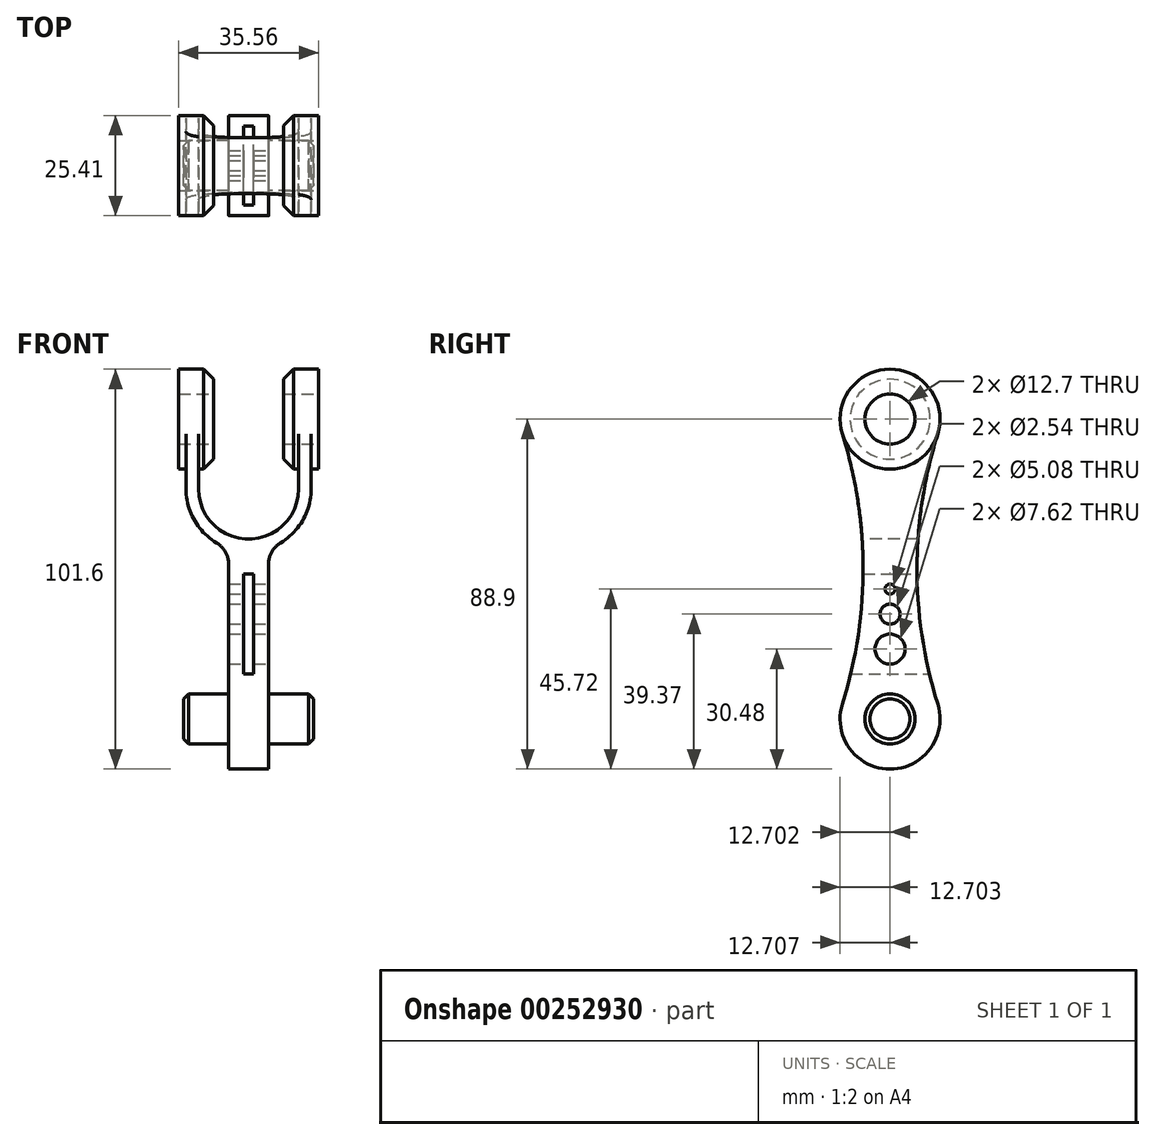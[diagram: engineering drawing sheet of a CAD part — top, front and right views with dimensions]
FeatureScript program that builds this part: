
annotation { "Feature Type Name" : "Feature", "Feature Type Description" : "" }
export const myFeature = defineFeature(function(context is Context, id is Id, definition is map)
    precondition{}
    {
        {
            var Q0;
            Q0=qCreatedBy(makeId("Front.planeOp"),FACE);
            var sketch = newSketch(context, id + "F0", { "sketchPlane" : qUnion([Q0])});
            skPoint(sketch, "E0.middle", {"position": v(0, 0) * mm});
            skArc(sketch, "E1", {"start": v(-8.17, -19.4) * mm, "mid": v(-13.82, -25.2) * mm, "end": v(-15.88, -33.02) * mm});
            skLineSegment(sketch, "E2.bottom", {"start": v(-5.08, 2.35) * mm, "end": v(5.08, 2.35) * mm});
            skLineSegment(sketch, "E2.left", {"start": v(-5.08, 2.35) * mm, "end": v(-5.08, -13.95) * mm});
            skLineSegment(sketch, "E2.right", {"start": v(5.08, 2.35) * mm, "end": v(5.08, -13.95) * mm});
            skArc(sketch, "E3", {"start": v(12.7, -33.02) * mm, "mid": v(0, -20.32) * mm, "end": v(-12.7, -33.02) * mm});
            skLineSegment(sketch, "E4.top", {"start": v(14.22, -50.8) * mm, "end": v(14.36, -50.8) * mm});
            skLineSegment(sketch, "E4.left", {"start": v(12.7, -33.02) * mm, "end": v(12.7, -49.28) * mm});
            skLineSegment(sketch, "E4.right", {"start": v(15.88, -33.02) * mm, "end": v(15.88, -49.28) * mm});
            skLineSegment(sketch, "E5.top", {"start": v(-14.36, -50.8) * mm, "end": v(-14.22, -50.8) * mm});
            skLineSegment(sketch, "E5.left", {"start": v(-15.88, -33.02) * mm, "end": v(-15.88, -49.28) * mm});
            skLineSegment(sketch, "E5.right", {"start": v(-12.7, -33.02) * mm, "end": v(-12.7, -49.28) * mm});
            skArc(sketch, "E6.trimOffspring", {"start": v(15.88, -33.02) * mm, "mid": v(13.82, -25.2) * mm, "end": v(8.17, -19.4) * mm});
            skPoint(sketch, "E7.visualSharp", {"position": v(-5.08, -17.97) * mm});
            skArc(sketch, "E7.filletArc", {"start": v(-8.17, -19.4) * mm, "mid": v(-5.9, -17.08) * mm, "end": v(-5.08, -13.95) * mm});
            skPoint(sketch, "E8.visualSharp", {"position": v(5.08, -17.97) * mm});
            skArc(sketch, "E8.filletArc", {"start": v(5.08, -13.95) * mm, "mid": v(5.9, -17.08) * mm, "end": v(8.17, -19.4) * mm});
            skArc(sketch, "E9.filletArc", {"start": v(12.7, -49.28) * mm, "mid": v(13.15, -50.35) * mm, "end": v(14.22, -50.8) * mm});
            skArc(sketch, "E10.filletArc", {"start": v(14.36, -50.8) * mm, "mid": v(15.44, -50.35) * mm, "end": v(15.88, -49.28) * mm});
            skArc(sketch, "E11.filletArc", {"start": v(-15.88, -49.28) * mm, "mid": v(-15.44, -50.35) * mm, "end": v(-14.36, -50.8) * mm});
            skArc(sketch, "E12.filletArc", {"start": v(-14.22, -50.8) * mm, "mid": v(-13.15, -50.35) * mm, "end": v(-12.7, -49.28) * mm});
            skSolve(sketch);
        }
        {
            var Q0;
            Q0=qSketchRegion(id+"F0",true);
            extrude(context, id + "F1", {"entities" : qUnion([Q0]), "endBound" : BoundingType.SYMMETRIC, "depth" : 38.1 * mm});
        }
        {
            var Q0;
            Q0=qCreatedBy(makeId("Right.planeOp"),FACE);
            var sketch = newSketch(context, id + "F2", { "sketchPlane" : qUnion([Q0])});
            skCircle(sketch, "E13", {"center": v(0, -50.8) * mm, "radius": 6.35 * mm});
            skSolve(sketch);
        }
        {
            var Q0;
            Q0=qCreatedBy(makeId("Right.planeOp"),FACE);
            var sketch = newSketch(context, id + "F3", { "sketchPlane" : qUnion([Q0])});
            skCircle(sketch, "E14", {"center": v(0, -50.8) * mm, "radius": 12.7 * mm});
            skSolve(sketch);
        }
        {
            var Q0;
            Q0 = qSketchRegion(id + "F3", true);
            extrude(context, id + "F4", {"entities" : qUnion([Q0]), "operationType" : NewBodyOperationType.ADD, "endBound" : BoundingType.SYMMETRIC, "depth" : 35.56 * mm});
        }
        {
            var Q0;
            Q0=qCreatedBy(makeId("Front.planeOp"),FACE);
            var sketch = newSketch(context, id + "F5", { "sketchPlane" : qUnion([Q0])});
            skLineSegment(sketch, "E15.bottom", {"start": v(8.9, -69.85) * mm, "end": v(-8.89, -69.85) * mm});
            skLineSegment(sketch, "E15.top", {"start": v(8.9, -31.75) * mm, "end": v(-8.89, -31.75) * mm});
            skLineSegment(sketch, "E15.left", {"start": v(8.9, -69.85) * mm, "end": v(8.9, -31.75) * mm});
            skLineSegment(sketch, "E15.right", {"start": v(-8.89, -69.85) * mm, "end": v(-8.89, -31.75) * mm});
            skPoint(sketch, "E15.middle", {"position": v(0, -50.8) * mm});
            skSolve(sketch);
        }
        {
            var Q0;
            Q0=qSketchRegion(id+"F2",true);
            extrude(context, id + "F6", {"entities" : qUnion([Q0]), "operationType" : NewBodyOperationType.REMOVE, "endBound" : BoundingType.SYMMETRIC, "oppositeDirection" : true, "depth" : 76.2 * mm});
        }
        {
            var Q0;
            Q0=qSketchRegion(id+"F5",true);
            extrude(context, id + "F7", {"entities" : qUnion([Q0]), "operationType" : NewBodyOperationType.REMOVE, "endBound" : BoundingType.SYMMETRIC, "oppositeDirection" : true, "depth" : 38.1 * mm});
        }
        {
            var Q0;
            Q0=makeQuery(id+"F7.boolean.opBoolean","INTERSECT",EDGE,{"derivedFrom":[makeQuery(id+"F4.opExtrude","SWEPT_FACE",FACE,{"disambiguationData":[OSD([sQuery(id+"F3.wireOp",EDGE,"E14")])]}),makeQuery(id+"F7.opExtrude","SWEPT_FACE",FACE,{"disambiguationData":[OSD([sQuery(id+"F5.wireOp",EDGE,"E15.right")])]})]});
            var Q1;
            Q1=makeQuery(id+"F7.boolean.opBoolean","INTERSECT",EDGE,{"derivedFrom":[makeQuery(id+"F4.opExtrude","SWEPT_FACE",FACE,{"disambiguationData":[OSD([sQuery(id+"F3.wireOp",EDGE,"E14")])]}),makeQuery(id+"F7.opExtrude","SWEPT_FACE",FACE,{"disambiguationData":[OSD([sQuery(id+"F5.wireOp",EDGE,"E15.left")])]})]});
            chamfer(context, id + "F8", {"entities" : qUnion([Q0, Q1]), "width" : 2.54 * mm, "tangentPropagation" : true});
        }
        {
            var Q0;
            Q0=qCreatedBy(makeId("Right.planeOp"),FACE);
            var sketch = newSketch(context, id + "F9", { "sketchPlane" : qUnion([Q0])});
            skArc(sketch, "E16", {"start": v(19.05, 25.39) * mm, "mid": v(0, 44.45) * mm, "end": v(-19.05, 25.39) * mm});
            skLineSegment(sketch, "E17.top", {"start": v(-19.05, -0.01) * mm, "end": v(19.05, -0.01) * mm});
            skLineSegment(sketch, "E17.left", {"start": v(-19.05, 25.39) * mm, "end": v(-19.05, -0.01) * mm});
            skLineSegment(sketch, "E17.right", {"start": v(19.05, 25.39) * mm, "end": v(19.05, -0.01) * mm});
            skSolve(sketch);
        }
        {
            var Q0;
            Q0=qSketchRegion(id+"F9",true);
            extrude(context, id + "F10", {"entities" : qUnion([Q0]), "operationType" : NewBodyOperationType.ADD, "endBound" : BoundingType.SYMMETRIC, "depth" : 10.16 * mm});
        }
        {
            var Q0;
            Q0=qCreatedBy(makeId("Right.planeOp"),FACE);
            var sketch = newSketch(context, id + "F11", { "sketchPlane" : qUnion([Q0])});
            skCircle(sketch, "E18", {"center": v(0, 25.4) * mm, "radius": 6.35 * mm});
            skSolve(sketch);
        }
        {
            var Q0;
            Q0=qSketchRegion(id+"F11",true);
            extrude(context, id + "F12", {"entities" : qUnion([Q0]), "operationType" : NewBodyOperationType.ADD, "endBound" : BoundingType.SYMMETRIC, "depth" : 33.02 * mm});
        }
        {
            var Q0;
            Q0=makeQuery(id+"F12.opExtrude","CAP_EDGE",EDGE,{"disambiguationData":[OSD([sQuery(id+"F11.wireOp",EDGE,"E18")])],"isStart":true});
            var Q1;
            Q1=makeQuery(id+"F12.opExtrude","CAP_EDGE",EDGE,{"disambiguationData":[OSD([sQuery(id+"F11.wireOp",EDGE,"E18")])],"isStart":false});
            chamfer(context, id + "F13", {"entities" : qUnion([Q0, Q1]), "width" : 1.27 * mm, "tangentPropagation" : true});
        }
        {
            var Q0;
            Q0=qCreatedBy(makeId("Right.planeOp"),FACE);
            var sketch = newSketch(context, id + "F14", { "sketchPlane" : qUnion([Q0])});
            skArc(sketch, "E19", {"start": v(12.12, 21.6) * mm, "mid": v(0, 38.1) * mm, "end": v(-12.12, 21.6) * mm});
            skArc(sketch, "E20", {"start": v(-12.12, -47) * mm, "mid": v(0, -63.5) * mm, "end": v(12.12, -47) * mm});
            skArc(sketch, "E21", {"start": v(12.12, 21.6) * mm, "mid": v(6.85, -12.7) * mm, "end": v(12.12, -47) * mm});
            skPoint(sketch, "E22.center.orphan", {"position": v(45.72, -6.35) * mm});
            skPoint(sketch, "E23.center.orphan", {"position": v(-45.72, -6.35) * mm});
            skArc(sketch, "E24", {"start": v(-12.12, -47) * mm, "mid": v(-6.85, -12.7) * mm, "end": v(-12.12, 21.6) * mm});
            skSolve(sketch);
        }
        {
            var Q0;
            Q0 = qSketchRegion(id + "F14", true);
            extrude(context, id + "F15", {"entities" : qUnion([Q0]), "operationType" : NewBodyOperationType.INTERSECT, "endBound" : BoundingType.SYMMETRIC, "depth" : 76.2 * mm});
        }
        {
            var Q0;
            Q0=qCreatedBy(makeId("Front.planeOp"),FACE);
            var sketch = newSketch(context, id + "F16", { "sketchPlane" : qUnion([Q0])});
            skLineSegment(sketch, "E25.bottom", {"start": v(-1.27, -11.4) * mm, "end": v(1.27, -11.4) * mm});
            skLineSegment(sketch, "E25.top", {"start": v(-1.27, 14) * mm, "end": v(1.27, 14) * mm});
            skLineSegment(sketch, "E25.left", {"start": v(-1.27, -11.4) * mm, "end": v(-1.27, 14) * mm});
            skLineSegment(sketch, "E25.right", {"start": v(1.27, -11.4) * mm, "end": v(1.27, 14) * mm});
            skSolve(sketch);
        }
        {
            var Q0;
            Q0=qSketchRegion(id+"F16",true);
            extrude(context, id + "F17", {"entities" : qUnion([Q0]), "operationType" : NewBodyOperationType.REMOVE, "endBound" : BoundingType.SYMMETRIC, "oppositeDirection" : true, "depth" : 50.8 * mm});
        }
        {
            var Q0;
            Q0=qCreatedBy(makeId("Right.planeOp"),FACE);
            var sketch = newSketch(context, id + "F18", { "sketchPlane" : qUnion([Q0])});
            skCircle(sketch, "E26", {"center": v(0, 7.62) * mm, "radius": 3.81 * mm});
            skCircle(sketch, "E27", {"center": v(0, -1.27) * mm, "radius": 2.54 * mm});
            skCircle(sketch, "E28", {"center": v(0, -7.62) * mm, "radius": 1.27 * mm});
            skSolve(sketch);
        }
        {
            var Q0;
            Q0=qSketchRegion(id+"F18",true);
            extrude(context, id + "F19", {"entities" : qUnion([Q0]), "operationType" : NewBodyOperationType.REMOVE, "endBound" : BoundingType.SYMMETRIC, "oppositeDirection" : true, "depth" : 25.4 * mm});
        }
        {
            var Q0;
            Q0=makeQuery(id+"F1.opExtrude","SWEPT_BODY",BODY,{"disambiguationData":[OSD([sQuery(id+"F0.wireOp",EDGE,"E1"),sQuery(id+"F0.wireOp",EDGE,"E2.bottom"),sQuery(id+"F0.wireOp",EDGE,"E2.left"),sQuery(id+"F0.wireOp",EDGE,"E2.right"),sQuery(id+"F0.wireOp",EDGE,"E3"),sQuery(id+"F0.wireOp",EDGE,"E4.top"),sQuery(id+"F0.wireOp",EDGE,"E4.left"),sQuery(id+"F0.wireOp",EDGE,"E4.right"),sQuery(id+"F0.wireOp",EDGE,"E5.top"),sQuery(id+"F0.wireOp",EDGE,"E5.left"),sQuery(id+"F0.wireOp",EDGE,"E5.right"),sQuery(id+"F0.wireOp",EDGE,"E6.trimOffspring"),sQuery(id+"F0.wireOp",EDGE,"E7.filletArc"),sQuery(id+"F0.wireOp",EDGE,"E8.filletArc"),sQuery(id+"F0.wireOp",EDGE,"E9.filletArc"),sQuery(id+"F0.wireOp",EDGE,"E10.filletArc"),sQuery(id+"F0.wireOp",EDGE,"E11.filletArc"),sQuery(id+"F0.wireOp",EDGE,"E12.filletArc")])]});
            var Q1;
            {var subQ0=sQuery(id+"F11.wireOp",EDGE,"E18");Q1=makeQuery(id+"F13.opChamfer","BLEND_EDGE",EDGE,{"blendedFrom":[makeQuery(id+"F12.opExtrude","CAP_EDGE",EDGE,{"disambiguationData":[OSD([subQ0])],"isStart":false}),makeQuery(id+"F12.boolean.opBoolean","SPLIT",FACE,{"disambiguationData":[TD([makeQuery(id+"F1.opExtrude","SWEPT_FACE",FACE,{"disambiguationData":[OSD([sQuery(id+"F0.wireOp",EDGE,"E2.right")])]})])],"derivedFrom":makeQuery(id+"F12.opExtrude","SWEPT_FACE",FACE,{"disambiguationData":[OSD([subQ0])]})})],"blendedInto":[makeQuery(id+"F12.boolean.opBoolean","SPLIT",FACE,{"disambiguationData":[TD([makeQuery(id+"F1.opExtrude","SWEPT_FACE",FACE,{"disambiguationData":[OSD([sQuery(id+"F0.wireOp",EDGE,"E2.right")])]})])],"derivedFrom":makeQuery(id+"F12.opExtrude","SWEPT_FACE",FACE,{"disambiguationData":[OSD([subQ0])]})})]});}
            transform(context, id + "F20", {"entities" : qUnion([Q0]), "transformType" : TransformType.ROTATION, "transformAxis" : qUnion([Q1]), "angle" : 3.14 * radian, "makeCopy" : false});
        }
        {
            var Q0;
            Q0=qCreatedBy(makeId("Front.planeOp"),FACE);
            var sketch = newSketch(context, id + "F21", { "sketchPlane" : qUnion([Q0])});
            skLineSegment(sketch, "E29", {"start": v(17.78, 101.6) * mm, "end": v(-17.78, 101.6) * mm, "construction": true});
            skLineSegment(sketch, "E30", {"start": v(0, 0) * mm, "end": v(0, 101.6) * mm, "construction": true});
            skSolve(sketch);
        }
        {
            var Q0;
            Q0=makeQuery(id+"F1.opExtrude","SWEPT_BODY",BODY,{"disambiguationData":[OSD([sQuery(id+"F0.wireOp",EDGE,"E1"),sQuery(id+"F0.wireOp",EDGE,"E2.bottom"),sQuery(id+"F0.wireOp",EDGE,"E2.left"),sQuery(id+"F0.wireOp",EDGE,"E2.right"),sQuery(id+"F0.wireOp",EDGE,"E3"),sQuery(id+"F0.wireOp",EDGE,"E4.top"),sQuery(id+"F0.wireOp",EDGE,"E4.left"),sQuery(id+"F0.wireOp",EDGE,"E4.right"),sQuery(id+"F0.wireOp",EDGE,"E5.top"),sQuery(id+"F0.wireOp",EDGE,"E5.left"),sQuery(id+"F0.wireOp",EDGE,"E5.right"),sQuery(id+"F0.wireOp",EDGE,"E6.trimOffspring"),sQuery(id+"F0.wireOp",EDGE,"E7.filletArc"),sQuery(id+"F0.wireOp",EDGE,"E8.filletArc"),sQuery(id+"F0.wireOp",EDGE,"E9.filletArc"),sQuery(id+"F0.wireOp",EDGE,"E10.filletArc"),sQuery(id+"F0.wireOp",EDGE,"E11.filletArc"),sQuery(id+"F0.wireOp",EDGE,"E12.filletArc")])]});
            var Q1;
            Q1=sQuery(id+"F21.wireOp",EDGE,"E30");
            transform(context, id + "F22", {"entities" : qUnion([Q0]), "transformType" : TransformType.TRANSLATION_ENTITY, "oppositeDirectionEntity" : true, "transformLine" : qUnion([Q1]), "makeCopy" : false});
        }
    });
